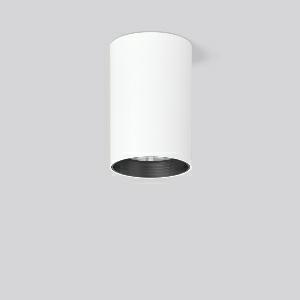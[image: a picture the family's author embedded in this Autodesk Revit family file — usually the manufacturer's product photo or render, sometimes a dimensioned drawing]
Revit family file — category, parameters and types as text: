
# Revit family: heledon_maxi_a_931227_002_3_4b7a
name_source: partatom
category: Lighting Fixtures
units: mm (PartAtom-declared; Revit-internal decimal feet)

## family parameters
Cut with Voids When Loaded = No
Host = Face
Light Source = No
Part Type = Normal
Room Calculation Point = No
Round Connector Dimension = Use Diameter
Shared = No

## types (1)
- HELEDON maxi A (1 x LED Modul 935, 3750 lm, 3500)
    Apparent Load = 35 VA
    Approval mark = CE
    CIE Flux Codes = 97 100 100 100 100
    Color Rendering = 92
    Color Temperature = 3500
    Default Elevation = 1800 mm
    Description = Series: HELEDON maxi
Cylindrical surface-mounted downlight. Housing: die-cast aluminium, powder-coated. Internal ceiling frame polycarbonate with bayonet mounting. Black plastic ring and recessed LED to prevent glare from the side. Optical assembly with lens made of plastic (polycarbonate) for the best homogeneous light distribution - can be changed without tools. Best colour rendering index Ra>90. Suitable for Ceiling mounting. Easy installation with a separate ceiling frame with bayonet mounting and plug connection. Driver integrated. Connected via plug-in connector. High quality converter without flickering and stroboscopic effect. The following accessories can be mounted without use of tools: interchangeable lenses, decorative glasses, honeycomb louvre, clear and frosted diffusers, white interchangeable plastic ring. 
Colour: traffic white, matt (RAL 9016)
Diameter: 123 mm
Height: 183 mm
Lamp: LED
Socket: without socket
Colour temperature: 3500K
Colour rendering index (CRI): 92
System power: 35 W
Rated luminous flux: 3750 lm
Luminous efficiency: 107 lm/W
Control gear: Regulated power supply
Protection class: I
Type of protection: IP 20
    Height = 183 mm
    Lamp = 1 x LED Modul 935
    Lamp Light Flux = 3750 lm
    Lamp count = 1
    Length = 123 mm
    Lifetime = 50000 h
    Luminous efficacy = 107 lm/W
    Manufacturer = RZB
    ModVariant = No
    Model = 931227.002.3
    Mounting Place = Ceiling
    Mounting Type = Surface mounted
    Number of Poles = 1
    OnlyDefault = Yes
    Power Factor = 1
    Product Name = HELEDON maxi A
    Product group = Surface mounted downlights
    ProductGroupID = 302
    Protection Class = Protection class I
    Protection Degree = IP 20
    RLX_Detail_Level = 1
    RLX_Emergency_Light_Flux = 0 lm
    RLX_Emergency_Type = 0
    RLX_Emergency_Type_DB = No
    RlxData = <blob elided: 97393 chars, md5=4cb56562>
    Socket = socket
    Standby Power = 0 W
    System Light Flux = 3750 lm
    System Power = 35 W
    Type Comments = Product without accessories
    Type Image = 931193.002.jpg
    URL = http://relux.com
    VarID = ---
    Voltage = 230 V
    Voltage Range = 220-240 V
    Weight = 0.00 kg
    Width = 0 mm  [stored 0 ft]

note: [stored X ft] marks values corroborated as IEEE doubles in the binary element streams (Revit-internal decimal feet)

## geometry (parser evidence)
native form markers: Blend x4, Sweep x9
no freeform markers — native parametric forms only
